# Revit family: Sideboard-Teknion-CFFTL-Figure_36H_Triple_Accomodation_FP_Cool_drawer_Low_Base-R2023
name_source: partatom
category: Furniture
units: mm (PartAtom-declared; Revit-internal decimal feet)

## family parameters
Always vertical = Yes
Cut with Voids When Loaded = No
Enable Cutting in Views = No
OmniClass Number = 23.40.20.00
OmniClass Title = General Furniture and Specialties
Render Appearance Source = Family Geometry
Room Calculation Point = No
Shared = Yes
Work Plane-Based = Yes

## types (2) — shared parameters
3 Door = Yes
AV Cutout = Yes
Assembly Code = E2020200
Default Elevation = 48 "
Depth = 26 "
Description = 36H Triple Sideboard, Accomodation FP & Cool Drawer, Low Base
Dim1 = 15 "
Doors1 = 16.95 "
Height = 37 "
Manufacturer = Teknion
Manufacturer Fax = 416.661.4586
Part Number = CFFTL
Product Documentation Link = https://d2r72yk5wmppdj.cloudfront.net
Product Line = Custom Wood
Product Page URL = https://www.teknion.com
Series = Figure
Sustainability Data = https://www.teknion.com
URL = www.teknion.com
Unit Weight URL = http://www.teknion.com
Warranty = http://www.teknion.com
Width = 72 "

## per-type parameters (varying)
| type | HFH | Model | WFW |
| (WFW) Waste/Cutouts for Fridge Drawer/ Waste | No | CFFTL_WFW | Yes |
| (HFH) H.Door/Cutouts for Fridge Drawer/ H.Door | Yes | CFFTL_HFH | No |

## geometry (parser evidence)
native form markers: Sweep x6
no freeform markers — native parametric forms only
